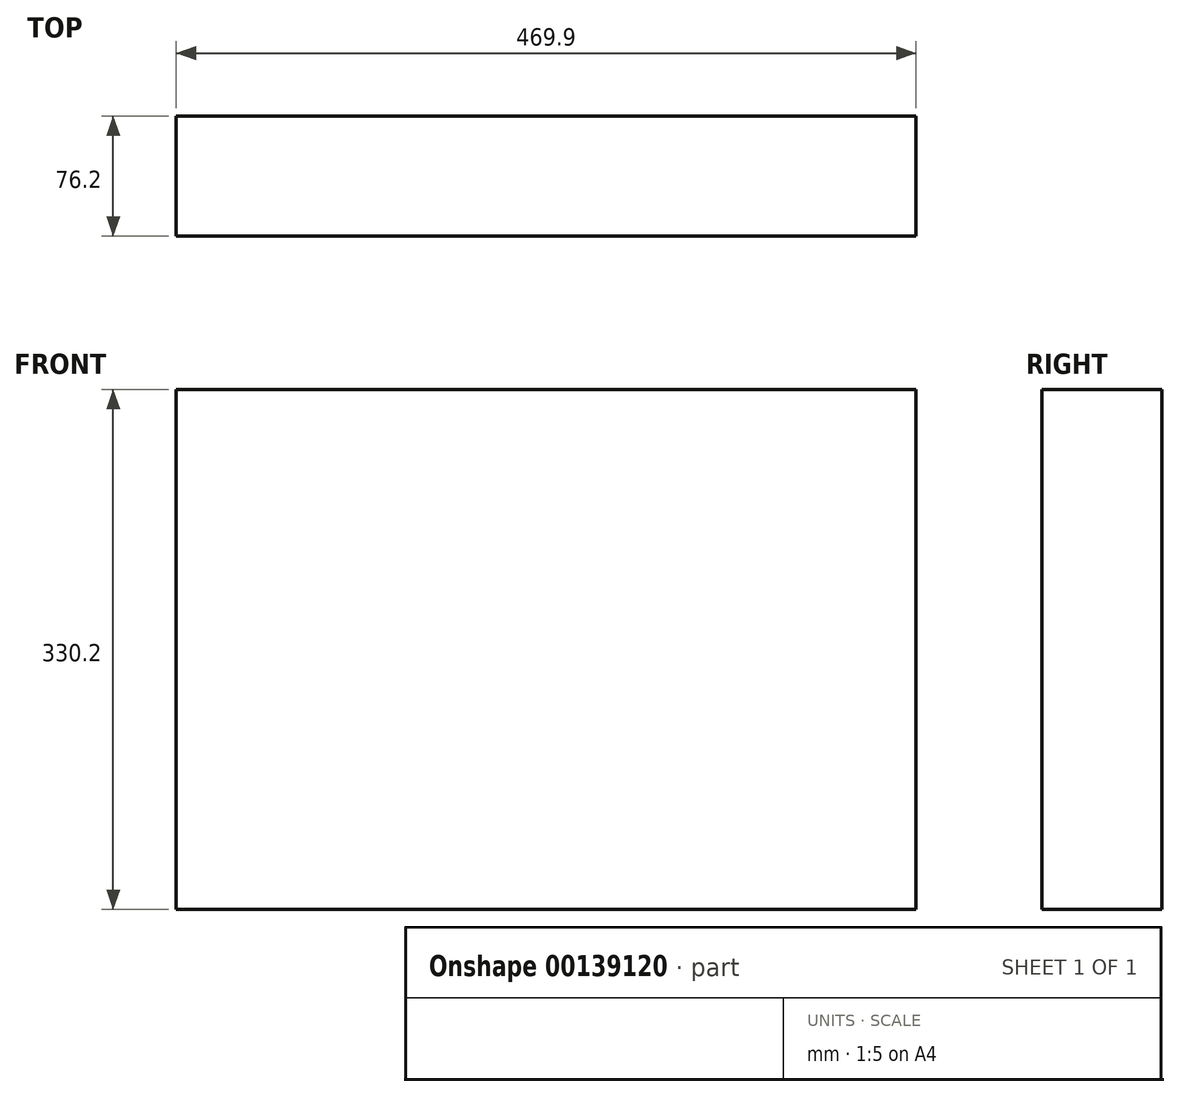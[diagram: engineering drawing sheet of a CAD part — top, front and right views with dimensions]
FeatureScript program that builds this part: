
annotation { "Feature Type Name" : "Feature", "Feature Type Description" : "" }
export const myFeature = defineFeature(function(context is Context, id is Id, definition is map)
    precondition{}
    {
        {
            var Q0;
            Q0=qCreatedBy(makeId("Front.planeOp"),FACE);
            var sketch = newSketch(context, id + "F0", { "sketchPlane" : qUnion([Q0])});
            skLineSegment(sketch, "E0.bottom", {"start": v(-234.95, 165.1) * mm, "end": v(234.95, 165.1) * mm});
            skLineSegment(sketch, "E0.top", {"start": v(-234.95, -165.1) * mm, "end": v(234.95, -165.1) * mm});
            skLineSegment(sketch, "E0.left", {"start": v(-234.95, 165.1) * mm, "end": v(-234.95, -165.1) * mm});
            skLineSegment(sketch, "E0.right", {"start": v(234.95, 165.1) * mm, "end": v(234.95, -165.1) * mm});
            skSolve(sketch);
        }
        {
            var Q0;
            Q0 = qSketchRegion(id + "F0", true);
            extrude(context, id + "F1", {"entities" : qUnion([Q0]), "depth" : 76.2 * mm});
        }
    });
